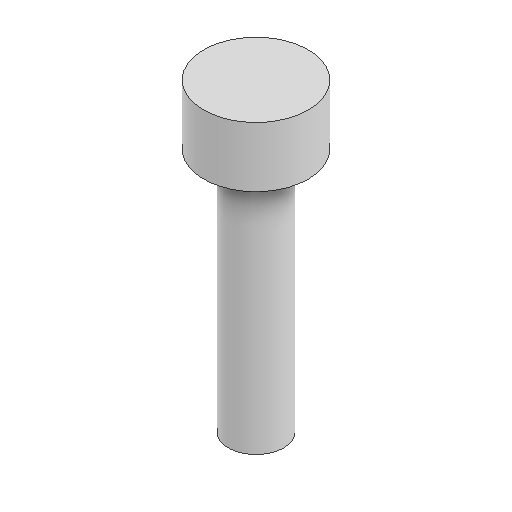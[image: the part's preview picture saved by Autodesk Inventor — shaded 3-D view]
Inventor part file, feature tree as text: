
AUTODESK INVENTOR PART (.ipt)
format: ipt  version: 2025 (Build 290162010, 162A)  size: 88,064 bytes
history: native  units: in
note: dims shown in document units (in); Inventor stores cm internally (conversion verified against a paired STEP export)
features: revolve x1, sketch x1
ambient origin geometry x8: Origin, YZ Plane, XZ Plane, XY Plane, X Axis, Y Axis, Z Axis, Center Point
bodies: Solid1 (feature_tree)
feature tree (2):
  revolve  "Revolution1"  [1 undecoded]
  sketch  "Sketch1"  dims[d1=0.265in d2=0.14in d3=0.152in d4=0.622in d5=90.0deg]
note: 1 required parameter value undecoded (feature->parameter linkage not recoverable at this tier; creation-order binding heuristic only, values carry confidence <= 0.55)
